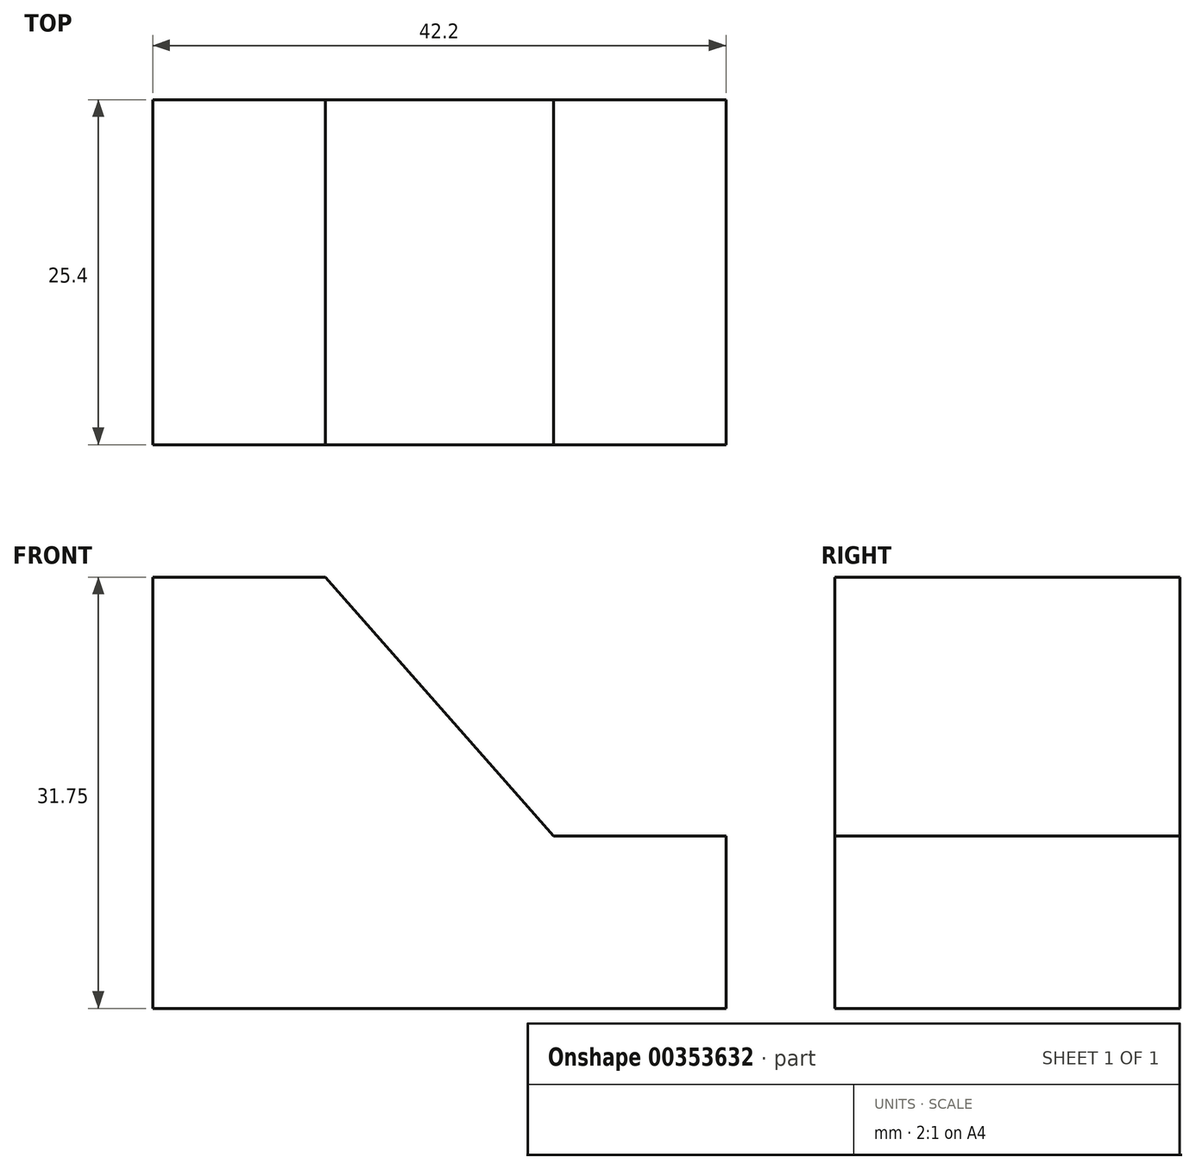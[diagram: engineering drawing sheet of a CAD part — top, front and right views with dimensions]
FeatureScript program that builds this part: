
annotation { "Feature Type Name" : "Feature", "Feature Type Description" : "" }
export const myFeature = defineFeature(function(context is Context, id is Id, definition is map)
    precondition{}
    {
        {
            var Q0;
            Q0=qCreatedBy(makeId("Front.planeOp"),FACE);
            var sketch = newSketch(context, id + "F0", { "sketchPlane" : qUnion([Q0])});
            skLineSegment(sketch, "E0", {"start": v(-31.02, 0) * mm, "end": v(-31.02, 31.75) * mm});
            skLineSegment(sketch, "E1", {"start": v(-31.02, 31.75) * mm, "end": v(-18.32, 31.75) * mm});
            skLineSegment(sketch, "E2", {"start": v(-18.32, 31.75) * mm, "end": v(-1.52, 12.7) * mm});
            skLineSegment(sketch, "E3", {"start": v(-1.52, 12.7) * mm, "end": v(11.18, 12.7) * mm});
            skLineSegment(sketch, "E4", {"start": v(11.18, 12.7) * mm, "end": v(11.18, 0) * mm});
            skLineSegment(sketch, "E5", {"start": v(11.18, 0) * mm, "end": v(-31.02, 0) * mm});
            skSolve(sketch);
        }
        {
            var Q0;
            Q0=makeQuery(id+"F0.imprint","IMPRINT",FACE,{"disambiguationData":[TD([[makeQuery(id+"F0.imprint","IMPRINT",EDGE,{"derivedFrom":sQuery(id+"F0.wireOp",EDGE,"E0")}),-1.0]])]});
            extrude(context, id + "F1", {"entities" : qUnion([Q0]), "depth" : 25.4 * mm});
        }
    });
